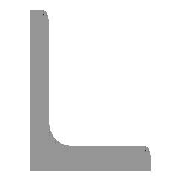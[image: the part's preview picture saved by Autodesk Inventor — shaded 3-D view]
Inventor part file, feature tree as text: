
AUTODESK INVENTOR PART (.ipt)
format: ipt  version: 2013 (Build 170138000, 138)  size: 129,024 bytes
history: native  units: mm (DEFAULTED — no unit token found)
features: other x4, plane x3, split x2, sketch x2
ambient origin geometry x8: Origin, YZ Plane, XZ Plane, XY Plane, X Axis, Y Axis, Z Axis, Center Point
bodies: Solid1 (feature_tree), Body (feature_tree)
feature tree (11):
  parser-record x1  (decoder bookkeeping rows leaked as tree rows — omitted from the tree; the rows remain in map.json)
  other  "Driven Length"
  other  "Start plane"
  other  "End plane"
  plane  "Work Plane4"
  split  "Split1"
  plane  "Work Plane5"
  split  "Split2"
  sketch  "Sketch3"  dims[d0=38.1mm]
  plane  "Work Plane3"
  sketch  "Sketch4"  dims[d1=38.1mm d2=4.7625mm d3=4.7625mm d4=1257.3mm d5=0.0mm d10=0.0mm d11=0.0mm d12=-0.0mm d13=1257.3mm d14=4.826mm d15=2.286mm d16=90.0deg d17=1257.3mm]
